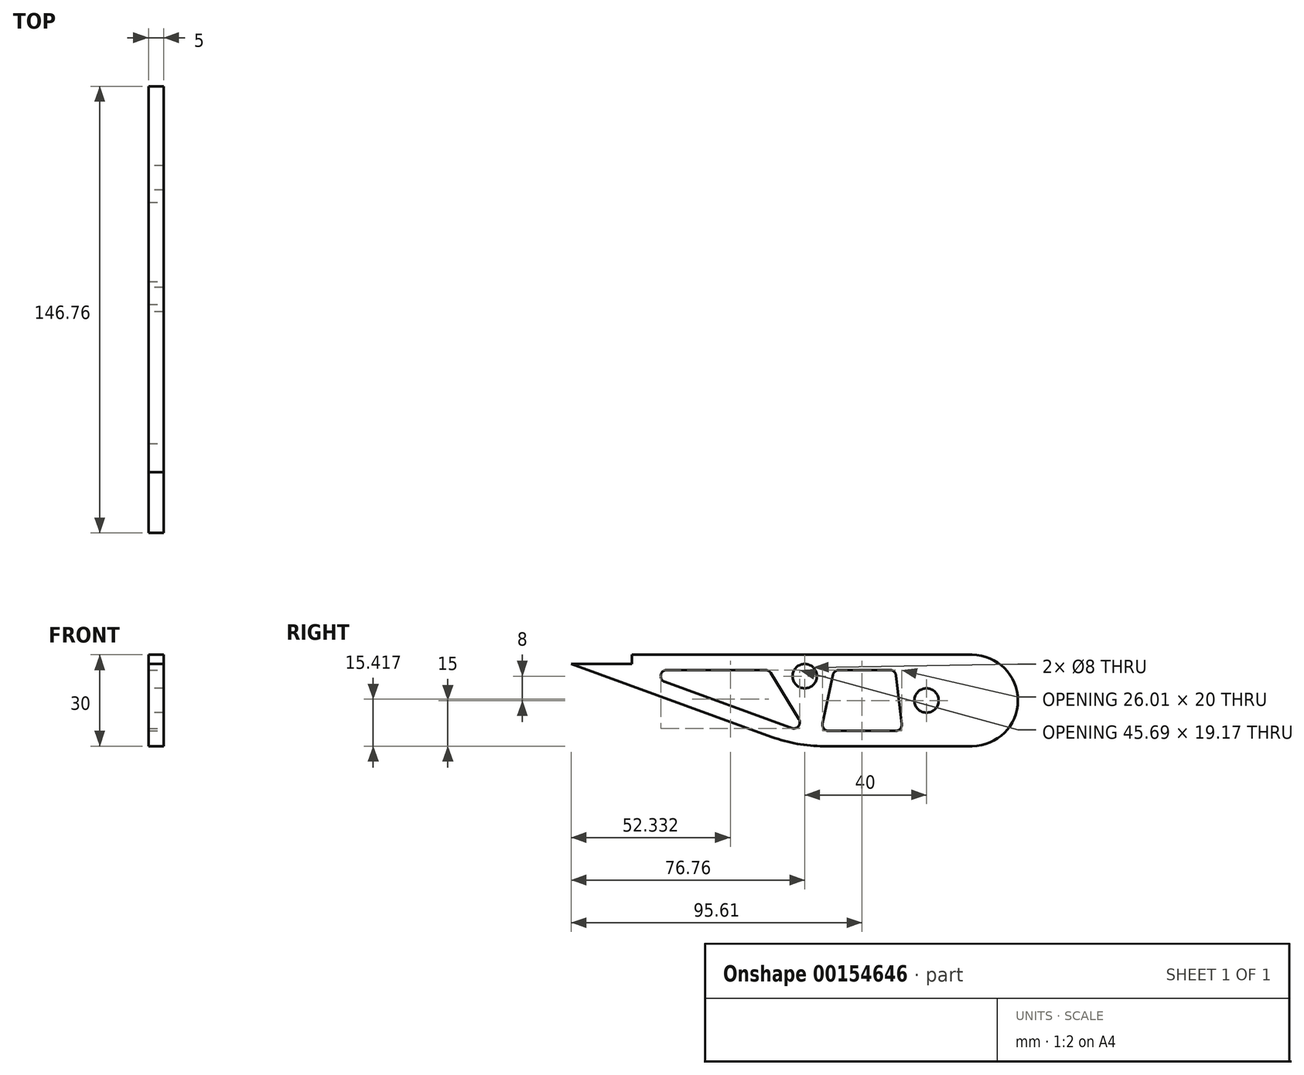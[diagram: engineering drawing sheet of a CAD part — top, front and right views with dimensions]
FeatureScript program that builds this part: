
annotation { "Feature Type Name" : "Feature", "Feature Type Description" : "" }
export const myFeature = defineFeature(function(context is Context, id is Id, definition is map)
    precondition{}
    {
        {
            var Q0;
            Q0=qCreatedBy(makeId("Right.planeOp"),FACE);
            var sketch = newSketch(context, id + "F0", { "sketchPlane" : qUnion([Q0])});
            skLineSegment(sketch, "E0.bottom", {"start": v(-61.76, 15) * mm, "end": v(50, 15) * mm});
            skLineSegment(sketch, "E0.top", {"start": v(1.24, -15) * mm, "end": v(50, -15) * mm});
            skArc(sketch, "E1", {"start": v(50, -15) * mm, "mid": v(65, 0) * mm, "end": v(50, 15) * mm});
            skLineSegment(sketch, "E2", {"start": v(-81.76, 12) * mm, "end": v(-15.86, -11.98) * mm});
            skCircle(sketch, "E3", {"center": v(35, 0) * mm, "radius": 4 * mm});
            skPoint(sketch, "E4.visualSharp", {"position": v(-7.58, -15) * mm});
            skArc(sketch, "E4.filletArc", {"start": v(-15.86, -11.98) * mm, "mid": v(-7.44, -14.24) * mm, "end": v(1.24, -15) * mm});
            skPoint(sketch, "E5.visualSharp", {"position": v(-90, 15) * mm});
            skCircle(sketch, "E6", {"center": v(-5, 8) * mm, "radius": 4 * mm});
            skLineSegment(sketch, "E7.top", {"start": v(-61.76, 12) * mm, "end": v(-81.76, 12) * mm});
            skLineSegment(sketch, "E7.left", {"start": v(-61.76, 15) * mm, "end": v(-61.76, 12) * mm});
            skSolve(sketch);
        }
        {
            var Q0;
            Q0=qSketchRegion(id+"F0",true);
            extrude(context, id + "F1", {"entities" : qUnion([Q0]), "depth" : 5 * mm});
        }
        {
            var Q0;
            Q0=makeQuery(id+"F1.opExtrude","CAP_FACE",FACE,{"disambiguationData":[OSD([sQuery(id+"F0.wireOp",EDGE,"E0.bottom"),sQuery(id+"F0.wireOp",EDGE,"E0.top"),sQuery(id+"F0.wireOp",EDGE,"E1"),sQuery(id+"F0.wireOp",EDGE,"E2"),sQuery(id+"F0.wireOp",EDGE,"E3"),sQuery(id+"F0.wireOp",EDGE,"E4.filletArc"),sQuery(id+"F0.wireOp",EDGE,"E5.filletArc"),sQuery(id+"F0.wireOp",EDGE,"E6")])],"isStart":false});
            var sketch = newSketch(context, id + "F2", { "sketchPlane" : qUnion([Q0])});
            skLineSegment(sketch, "E8", {"start": v(-50.3, 10) * mm, "end": v(-17.92, 10) * mm});
            skLineSegment(sketch, "E9", {"start": v(-16.21, 9.05) * mm, "end": v(-6.88, -6.12) * mm});
            skLineSegment(sketch, "E10", {"start": v(6.25, 10) * mm, "end": v(22.98, 10) * mm});
            skLineSegment(sketch, "E11", {"start": v(24.97, 8.23) * mm, "end": v(26.85, -7.77) * mm});
            skLineSegment(sketch, "E12", {"start": v(24.86, -10) * mm, "end": v(2.84, -10) * mm});
            skLineSegment(sketch, "E13", {"start": v(0.89, -7.58) * mm, "end": v(4.29, 8.42) * mm});
            skPoint(sketch, "E14.visualSharp", {"position": v(27.11, -10) * mm});
            skArc(sketch, "E14.filletArc", {"start": v(24.86, -10) * mm, "mid": v(26.36, -9.33) * mm, "end": v(26.85, -7.77) * mm});
            skPoint(sketch, "E15.visualSharp", {"position": v(24.76, 10) * mm});
            skArc(sketch, "E15.filletArc", {"start": v(24.97, 8.23) * mm, "mid": v(24.31, 9.5) * mm, "end": v(22.98, 10) * mm});
            skPoint(sketch, "E16.visualSharp", {"position": v(4.63, 10) * mm});
            skArc(sketch, "E16.filletArc", {"start": v(6.25, 10) * mm, "mid": v(4.99, 9.55) * mm, "end": v(4.29, 8.42) * mm});
            skPoint(sketch, "E17.visualSharp", {"position": v(0.38, -10) * mm});
            skArc(sketch, "E17.filletArc", {"start": v(0.89, -7.58) * mm, "mid": v(1.3, -9.26) * mm, "end": v(2.84, -10) * mm});
            skPoint(sketch, "E18.visualSharp", {"position": v(-6.25, -7.14) * mm});
            skPoint(sketch, "E19.visualSharp", {"position": v(-16.8, 10) * mm});
            skArc(sketch, "E19.filletArc", {"start": v(-16.21, 9.05) * mm, "mid": v(-16.94, 9.75) * mm, "end": v(-17.92, 10) * mm});
            skPoint(sketch, "E20.visualSharp", {"position": v(-31.12, 10) * mm});
            skLineSegment(sketch, "E21", {"start": v(-50.99, 6.12) * mm, "end": v(-10, -8.8) * mm});
            skArc(sketch, "E22.filletArc", {"start": v(-50.3, 10) * mm, "mid": v(-52.27, 8.35) * mm, "end": v(-50.99, 6.12) * mm});
            skPoint(sketch, "E23.visualSharp", {"position": v(-6.7, -10) * mm});
            skArc(sketch, "E23.filletArc", {"start": v(-10, -8.8) * mm, "mid": v(-9.6, -8.94) * mm, "end": v(-9.18, -9.07) * mm});
            skPoint(sketch, "E24.visualSharp", {"position": v(-4.49, -10) * mm});
            skPoint(sketch, "E25.visualSharp", {"position": v(44, 10) * mm});
            skPoint(sketch, "E26.visualSharp", {"position": v(44, -10) * mm});
            skArc(sketch, "E27.filletArc", {"start": v(-9.18, -9.07) * mm, "mid": v(-7, -8.4) * mm, "end": v(-6.88, -6.12) * mm});
            skPoint(sketch, "E28.top.end.orphan", {"position": v(50, -10) * mm});
            skSolve(sketch);
        }
        {
            var Q0;
            Q0 = qSketchRegion(id + "F2", true);
            extrude(context, id + "F3", {"entities" : qUnion([Q0]), "operationType" : NewBodyOperationType.REMOVE, "oppositeDirection" : true, "depth" : 25 * mm});
        }
    });
